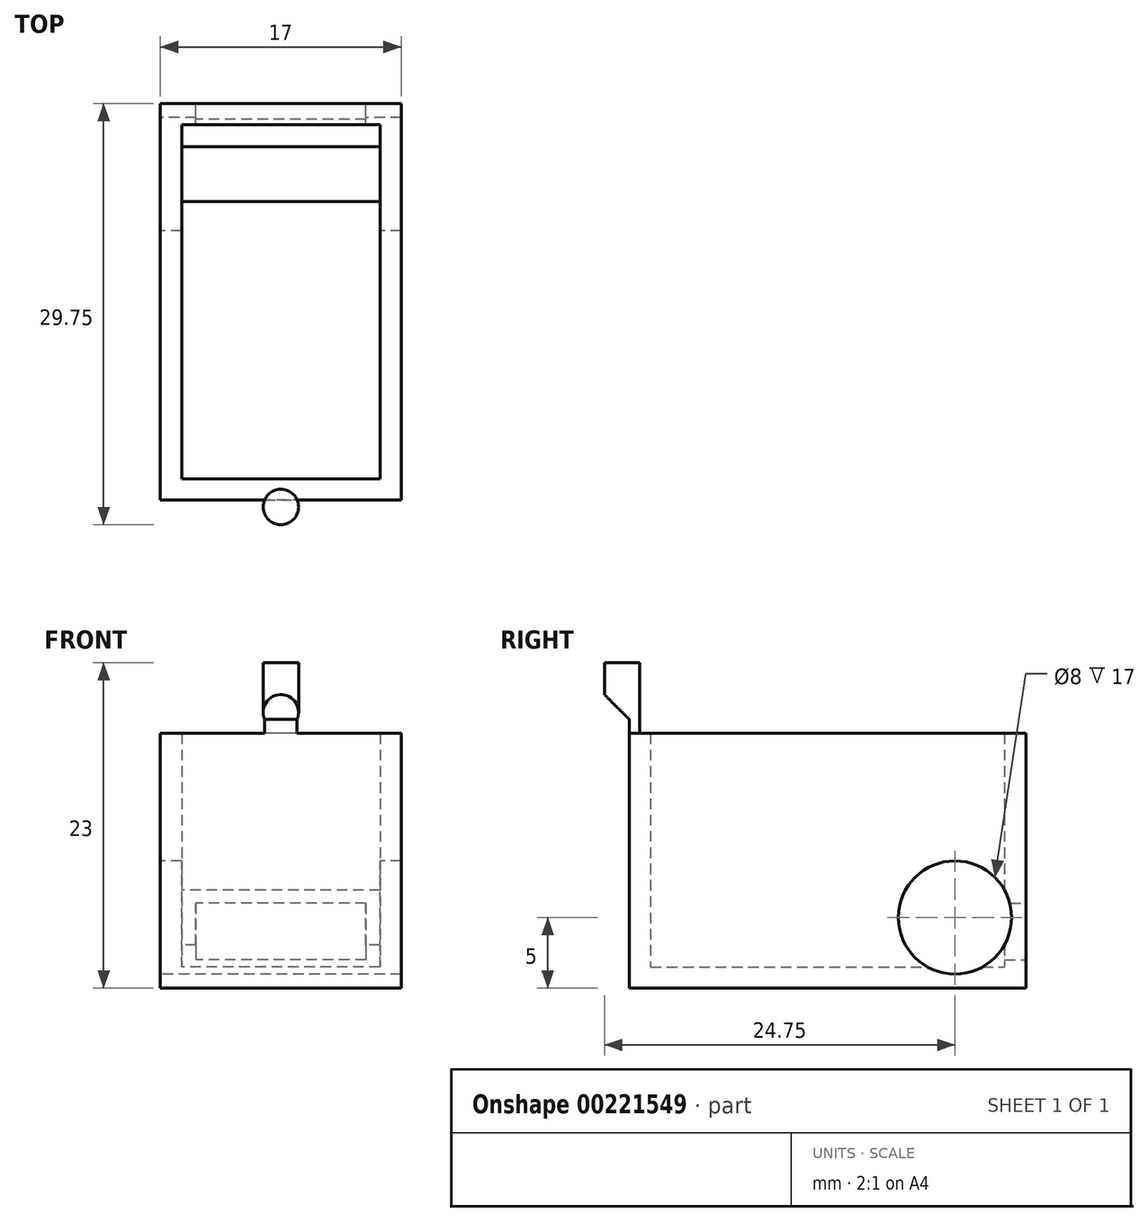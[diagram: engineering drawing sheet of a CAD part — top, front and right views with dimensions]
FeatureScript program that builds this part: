
annotation { "Feature Type Name" : "Feature", "Feature Type Description" : "" }
export const myFeature = defineFeature(function(context is Context, id is Id, definition is map)
    precondition{}
    {
        {
            var Q0;
            Q0=qCreatedBy(makeId("Top.planeOp"),FACE);
            var sketch = newSketch(context, id + "F0", { "sketchPlane" : qUnion([Q0])});
            skLineSegment(sketch, "E0.bottom", {"start": v(7, -12.5) * mm, "end": v(-7, -12.5) * mm});
            skLineSegment(sketch, "E0.top", {"start": v(7, 12.5) * mm, "end": v(-7, 12.5) * mm});
            skLineSegment(sketch, "E0.left", {"start": v(7, -12.5) * mm, "end": v(7, 12.5) * mm});
            skLineSegment(sketch, "E0.right", {"start": v(-7, -12.5) * mm, "end": v(-7, 12.5) * mm});
            skPoint(sketch, "E0.middle", {"position": v(0, 0) * mm});
            skLineSegment(sketch, "E1.bottom", {"start": v(8.5, -14) * mm, "end": v(-8.5, -14) * mm});
            skLineSegment(sketch, "E1.top", {"start": v(8.5, 14) * mm, "end": v(-8.5, 14) * mm});
            skLineSegment(sketch, "E1.left", {"start": v(8.5, -14) * mm, "end": v(8.5, 14) * mm});
            skLineSegment(sketch, "E1.right", {"start": v(-8.5, -14) * mm, "end": v(-8.5, 14) * mm});
            skSolve(sketch);
        }
        {
            var Q0;
            Q0=makeQuery(id+"F0.imprint","IMPRINT",FACE,{"disambiguationData":[TD([[makeQuery(id+"F0.imprint","IMPRINT",EDGE,{"derivedFrom":sQuery(id+"F0.wireOp",EDGE,"E0.bottom")}),1.0]])]});
            extrude(context, id + "F1", {"entities" : qUnion([Q0]), "depth" : 23 * mm});
        }
        {
            var Q0;
            Q0=makeQuery(id+"F0.imprint","IMPRINT",FACE,{"disambiguationData":[TD([[makeQuery(id+"F0.imprint","IMPRINT",EDGE,{"derivedFrom":sQuery(id+"F0.wireOp",EDGE,"E0.bottom")}),-1.0]])]});
            extrude(context, id + "F2", {"entities" : qUnion([Q0]), "operationType" : NewBodyOperationType.ADD, "depth" : 1.5 * mm});
        }
        {
            var Q0;
            Q0=makeQuery(id+"F1.opExtrude","SWEPT_FACE",FACE,{"disambiguationData":[OSD([sQuery(id+"F0.wireOp",EDGE,"E1.bottom")])]});
            var sketch = newSketch(context, id + "F3", { "sketchPlane" : qUnion([Q0])});
            skLineSegment(sketch, "E2.bottom", {"start": v(-8.5, 23) * mm, "end": v(8.5, 23) * mm});
            skLineSegment(sketch, "E2.top", {"start": v(-8.5, 19) * mm, "end": v(8.5, 19) * mm});
            skLineSegment(sketch, "E2.left", {"start": v(-8.5, 23) * mm, "end": v(-8.5, 19) * mm});
            skLineSegment(sketch, "E2.right", {"start": v(8.5, 23) * mm, "end": v(8.5, 19) * mm});
            skSolve(sketch);
        }
        {
            var Q0;
            Q0=makeQuery(id+"F3.imprint","IMPRINT",FACE,{"disambiguationData":[TD([[makeQuery(id+"F3.imprint","IMPRINT",EDGE,{"derivedFrom":sQuery(id+"F3.wireOp",EDGE,"E2.bottom")}),1.0]])]});
            extrude(context, id + "F4", {"entities" : qUnion([Q0]), "operationType" : NewBodyOperationType.ADD, "depth" : 4 * mm});
        }
        {
            var Q0;
            Q0=makeQuery(id+"F1.opExtrude","SWEPT_FACE",FACE,{"disambiguationData":[OSD([sQuery(id+"F0.wireOp",EDGE,"E1.top")])]});
            var sketch = newSketch(context, id + "F5", { "sketchPlane" : qUnion([Q0])});
            skLineSegment(sketch, "E3.bottom", {"start": v(-8.5, 23) * mm, "end": v(8.5, 23) * mm});
            skLineSegment(sketch, "E3.top", {"start": v(-8.5, 19) * mm, "end": v(8.5, 19) * mm});
            skLineSegment(sketch, "E3.left", {"start": v(-8.5, 23) * mm, "end": v(-8.5, 19) * mm});
            skLineSegment(sketch, "E3.right", {"start": v(8.5, 23) * mm, "end": v(8.5, 19) * mm});
            skLineSegment(sketch, "E4.bottom", {"start": v(-6, 6) * mm, "end": v(6, 6) * mm});
            skLineSegment(sketch, "E4.top", {"start": v(-6, 2) * mm, "end": v(6, 2) * mm});
            skLineSegment(sketch, "E4.left", {"start": v(-6, 6) * mm, "end": v(-6, 2) * mm});
            skLineSegment(sketch, "E4.right", {"start": v(6, 6) * mm, "end": v(6, 2) * mm});
            skSolve(sketch);
        }
        {
            var Q0;
            Q0=makeQuery(id+"F5.imprint","IMPRINT",FACE,{"disambiguationData":[TD([[makeQuery(id+"F5.imprint","IMPRINT",EDGE,{"derivedFrom":sQuery(id+"F5.wireOp",EDGE,"E3.bottom")}),-1.0]])]});
            extrude(context, id + "F6", {"entities" : qUnion([Q0]), "operationType" : NewBodyOperationType.ADD, "depth" : 4 * mm});
        }
        {
            var Q0;
            Q0=makeQuery(id+"F5.imprint","IMPRINT",FACE,{"disambiguationData":[TD([[makeQuery(id+"F5.imprint","IMPRINT",EDGE,{"derivedFrom":sQuery(id+"F5.wireOp",EDGE,"E4.bottom")}),-1.0]])]});
            extrude(context, id + "F7", {"entities" : qUnion([Q0]), "operationType" : NewBodyOperationType.REMOVE, "endBound" : BoundingType.UP_TO_NEXT, "oppositeDirection" : true, "depth" : 25 * mm});
        }
        {
            var Q0;
            Q0=makeQuery(id+"F6.opExtrude","CAP_EDGE",EDGE,{"disambiguationData":[OSD([sQuery(id+"F5.wireOp",EDGE,"E3.top")])],"isStart":false});
            var Q1;
            Q1=makeQuery(id+"F4.opExtrude","CAP_EDGE",EDGE,{"disambiguationData":[OSD([sQuery(id+"F3.wireOp",EDGE,"E2.top")])],"isStart":false});
            chamfer(context, id + "F8", {"entities" : qUnion([Q0, Q1]), "width" : 4 * mm, "tangentPropagation" : true});
        }
        {
            var Q0;
            Q0=makeQuery(id+"F6.boolean.opBoolean","MERGE",FACE,{"derivedFrom":[makeQuery(id+"F4.boolean.opBoolean","MERGE",FACE,{"derivedFrom":[makeQuery(id+"F1.opExtrude","CAP_FACE",FACE,{"disambiguationData":[OSD([sQuery(id+"F0.wireOp",EDGE,"E0.bottom"),sQuery(id+"F0.wireOp",EDGE,"E0.top"),sQuery(id+"F0.wireOp",EDGE,"E0.left"),sQuery(id+"F0.wireOp",EDGE,"E0.right"),sQuery(id+"F0.wireOp",EDGE,"E1.bottom"),sQuery(id+"F0.wireOp",EDGE,"E1.top"),sQuery(id+"F0.wireOp",EDGE,"E1.left"),sQuery(id+"F0.wireOp",EDGE,"E1.right")])],"isStart":false}),makeQuery(id+"F4.opExtrude","SWEPT_FACE",FACE,{"disambiguationData":[OSD([sQuery(id+"F3.wireOp",EDGE,"E2.bottom")])]})]}),makeQuery(id+"F6.opExtrude","SWEPT_FACE",FACE,{"disambiguationData":[OSD([sQuery(id+"F5.wireOp",EDGE,"E3.bottom")])]})]});
            var sketch = newSketch(context, id + "F9", { "sketchPlane" : qUnion([Q0])});
            skCircle(sketch, "E5", {"center": v(0, 14.5) * mm, "radius": 1.25 * mm});
            skCircle(sketch, "E6.MirrorC", {"center": v(0, -14.5) * mm, "radius": 1.25 * mm});
            skSolve(sketch);
        }
        {
            var Q0;
            Q0=makeQuery(id+"F9.imprint","IMPRINT",FACE,{"disambiguationData":[TD([[makeQuery(id+"F9.imprint","IMPRINT",EDGE,{"derivedFrom":sQuery(id+"F9.wireOp",EDGE,"E5")}),1.0]])]});
            var Q1;
            Q1=makeQuery(id+"F9.imprint","IMPRINT",FACE,{"disambiguationData":[TD([[makeQuery(id+"F9.imprint","IMPRINT",EDGE,{"derivedFrom":sQuery(id+"F9.wireOp",EDGE,"E6.MirrorC")}),-1.0]])]});
            extrude(context, id + "F10", {"entities" : qUnion([Q0, Q1]), "operationType" : NewBodyOperationType.REMOVE, "oppositeDirection" : true, "depth" : 5 * mm});
        }
        {
            var Q0;
            Q0=makeQuery(id+"F6.boolean.opBoolean","MERGE",FACE,{"derivedFrom":[makeQuery(id+"F4.boolean.opBoolean","MERGE",FACE,{"derivedFrom":[makeQuery(id+"F1.opExtrude","SWEPT_FACE",FACE,{"disambiguationData":[OSD([sQuery(id+"F0.wireOp",EDGE,"E1.right")])]}),makeQuery(id+"F4.opExtrude","SWEPT_FACE",FACE,{"disambiguationData":[OSD([sQuery(id+"F3.wireOp",EDGE,"E2.left")])]})]}),makeQuery(id+"F6.opExtrude","SWEPT_FACE",FACE,{"disambiguationData":[OSD([sQuery(id+"F5.wireOp",EDGE,"E3.right")])]})]});
            var sketch = newSketch(context, id + "F11", { "sketchPlane" : qUnion([Q0])});
            skCircle(sketch, "E7", {"center": v(-9, 5) * mm, "radius": 4 * mm});
            skSolve(sketch);
        }
        {
            var Q0;
            Q0=makeQuery(id+"F11.imprint","IMPRINT",FACE,{"disambiguationData":[TD([[makeQuery(id+"F11.imprint","IMPRINT",EDGE,{"derivedFrom":sQuery(id+"F11.wireOp",EDGE,"E7")}),1.0]])]});
            extrude(context, id + "F12", {"entities" : qUnion([Q0]), "operationType" : NewBodyOperationType.REMOVE, "oppositeDirection" : true, "depth" : 25 * mm});
        }
    });
